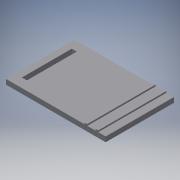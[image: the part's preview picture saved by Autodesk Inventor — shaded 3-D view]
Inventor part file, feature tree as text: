
AUTODESK INVENTOR PART (.ipt)
format: ipt  version: 2018.3 (Build 223284000, 284)  size: 122,880 bytes
history: native  units: mm
features: extrude x3, sketch x3
ambient origin geometry x8: Origin, YZ Plane, XZ Plane, XY Plane, X Axis, Y Axis, Z Axis, Center Point
bodies: Solid1 (feature_tree)
feature tree (6):
  extrude  "Extrusion1"  Depth=13.7mm
  extrude  "Extrusion2"  Depth=1.0mm
  extrude  "Extrusion3"  Depth=1.8mm
  sketch  "Sketch1"  dims[d0=20.0mm d1=13.7mm]
  sketch  "Sketch2"  dims[d2=1.0mm d3=0.0mm d4=1.0mm]
  sketch  "Sketch3"  dims[d5=1.0mm d6=1.8mm d7=0.8mm d8=0.0mm d9=3.5mm d10=1.0mm d11=10.0mm d12=10.0mm d13=0.0mm d14=1.85mm d15=1.85mm]
